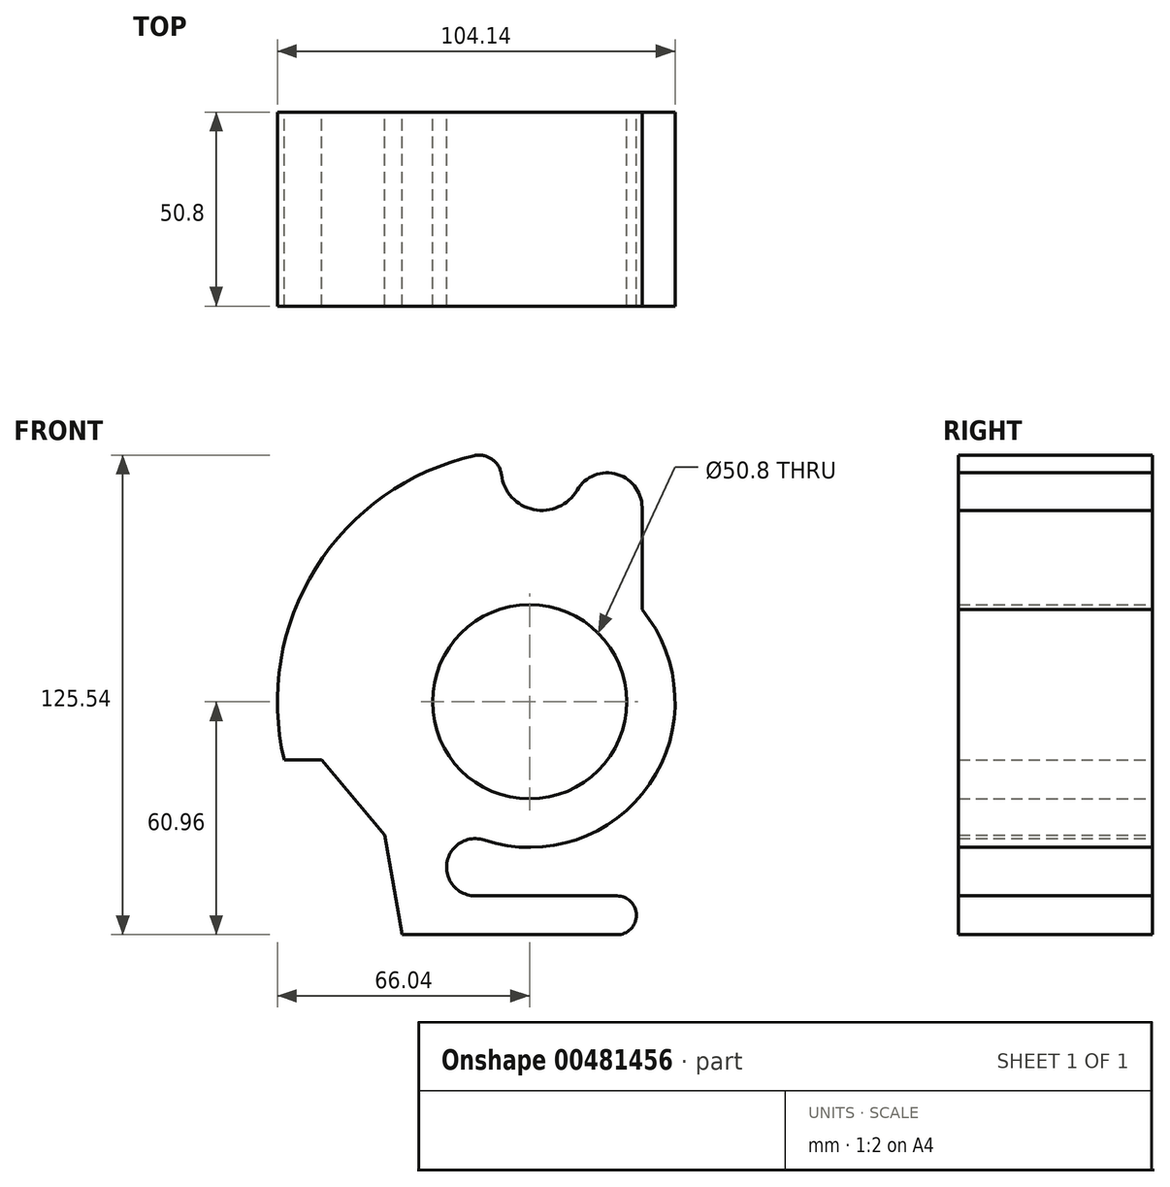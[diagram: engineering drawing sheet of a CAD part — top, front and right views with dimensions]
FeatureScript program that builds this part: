
annotation { "Feature Type Name" : "Feature", "Feature Type Description" : "" }
export const myFeature = defineFeature(function(context is Context, id is Id, definition is map)
    precondition{}
    {
        {
            var Q0;
            Q0=qCreatedBy(makeId("Front.planeOp"),FACE);
            var sketch = newSketch(context, id + "F0", { "sketchPlane" : qUnion([Q0])});
            skCircle(sketch, "E0", {"center": v(0, 0) * mm, "radius": 25.4 * mm});
            skArc(sketch, "E1", {"start": v(-11.9, -36.2) * mm, "mid": v(31.44, -21.53) * mm, "end": v(29.44, 24.19) * mm});
            skArc(sketch, "E2", {"start": v(29.44, 50.11) * mm, "mid": v(23.04, 59.53) * mm, "end": v(12.42, 55.4) * mm});
            skArc(sketch, "E3", {"start": v(-7.38, 59.46) * mm, "mid": v(1.07, 50.33) * mm, "end": v(12.42, 55.4) * mm});
            skArc(sketch, "E4", {"start": v(-14.46, 64.44) * mm, "mid": v(-56, 35) * mm, "end": v(-64.26, -15.24) * mm});
            skLineSegment(sketch, "E5", {"start": v(-64.26, -15.24) * mm, "end": v(-54.42, -15.24) * mm});
            skLineSegment(sketch, "E6", {"start": v(-54.42, -15.24) * mm, "end": v(-37.96, -34.86) * mm});
            skLineSegment(sketch, "E7", {"start": v(-37.96, -34.86) * mm, "end": v(-33.36, -60.96) * mm});
            skLineSegment(sketch, "E8", {"start": v(-33.36, -60.96) * mm, "end": v(22.86, -60.96) * mm});
            skLineSegment(sketch, "E9", {"start": v(27.94, -60.96) * mm, "end": v(27.94, -50.8) * mm, "construction": true});
            skLineSegment(sketch, "E10", {"start": v(22.86, -50.8) * mm, "end": v(-14.25, -50.8) * mm});
            skLineSegment(sketch, "E11", {"start": v(-24.37, 50.11) * mm, "end": v(46.79, 50.11) * mm, "construction": true});
            skLineSegment(sketch, "E12", {"start": v(29.44, 50.11) * mm, "end": v(29.44, 24.19) * mm});
            skPoint(sketch, "E13.visualSharp", {"position": v(-6.24, 65.74) * mm});
            skArc(sketch, "E13.filletArc", {"start": v(-7.38, 59.46) * mm, "mid": v(-9.82, 63.52) * mm, "end": v(-14.46, 64.44) * mm});
            skArc(sketch, "E14", {"start": v(-11.9, -36.2) * mm, "mid": v(-21.65, -42.12) * mm, "end": v(-14.25, -50.8) * mm});
            skPoint(sketch, "E14.first.point", {"position": v(-11.9, -36.2) * mm});
            skPoint(sketch, "E14.third.point", {"position": v(-14.25, -50.8) * mm});
            skLineSegment(sketch, "E15", {"start": v(-21.74, -34.58) * mm, "end": v(-21.74, -68.26) * mm, "construction": true});
            skArc(sketch, "E16", {"start": v(22.86, -60.96) * mm, "mid": v(27.94, -55.88) * mm, "end": v(22.86, -50.8) * mm});
            skSolve(sketch);
        }
        {
            var Q0;
            Q0=makeQuery(id+"F0.imprint","IMPRINT",FACE,{"disambiguationData":[TD([[makeQuery(id+"F0.imprint","IMPRINT",EDGE,{"derivedFrom":sQuery(id+"F0.wireOp",EDGE,"E0")}),-1.0]])]});
            extrude(context, id + "F1", {"entities" : qUnion([Q0]), "depth" : 50.8 * mm, "offsetDistance" : 25.4 * mm});
        }
    });
